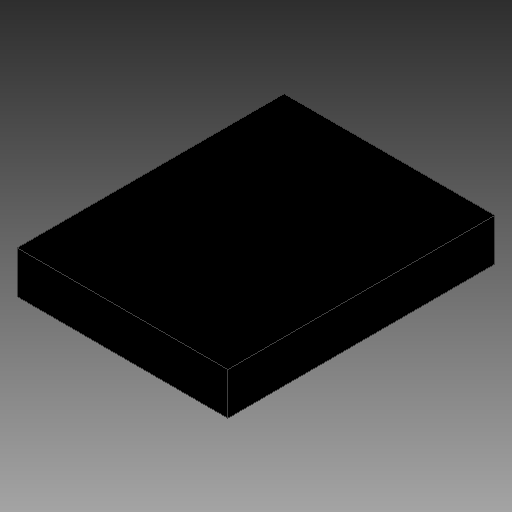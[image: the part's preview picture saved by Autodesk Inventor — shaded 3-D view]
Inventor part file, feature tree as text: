
AUTODESK INVENTOR PART (.ipt)
format: ipt  version: 2017 (Build 210142000, 142)  size: 107,520 bytes
history: native  units: in
note: dims shown in document units (in); Inventor stores cm internally (conversion verified against a paired STEP export)
features: extrude x2, sketch x2
ambient origin geometry x8: Origin, YZ Plane, XZ Plane, XY Plane, X Axis, Y Axis, Z Axis, Center Point
bodies: Solid1 (feature_tree)
feature tree (4):
  extrude  "Extrusion1"  Depth=9.5in
  extrude  "Extrusion2"  Depth=0.1in
  sketch  "Sketch1"  dims[d0=7.5in d1=9.5in]
  sketch  "Sketch2"  dims[d2=1.5in d3=0.0in d4=0.2in d5=2.1875in d6=3.3125in d7=0.2in d8=0.2in d9=2.9375in d10=2.9375in d11=0.2in d12=2.9375in d13=2.9375in d14=0.1in d15=0.0in]
